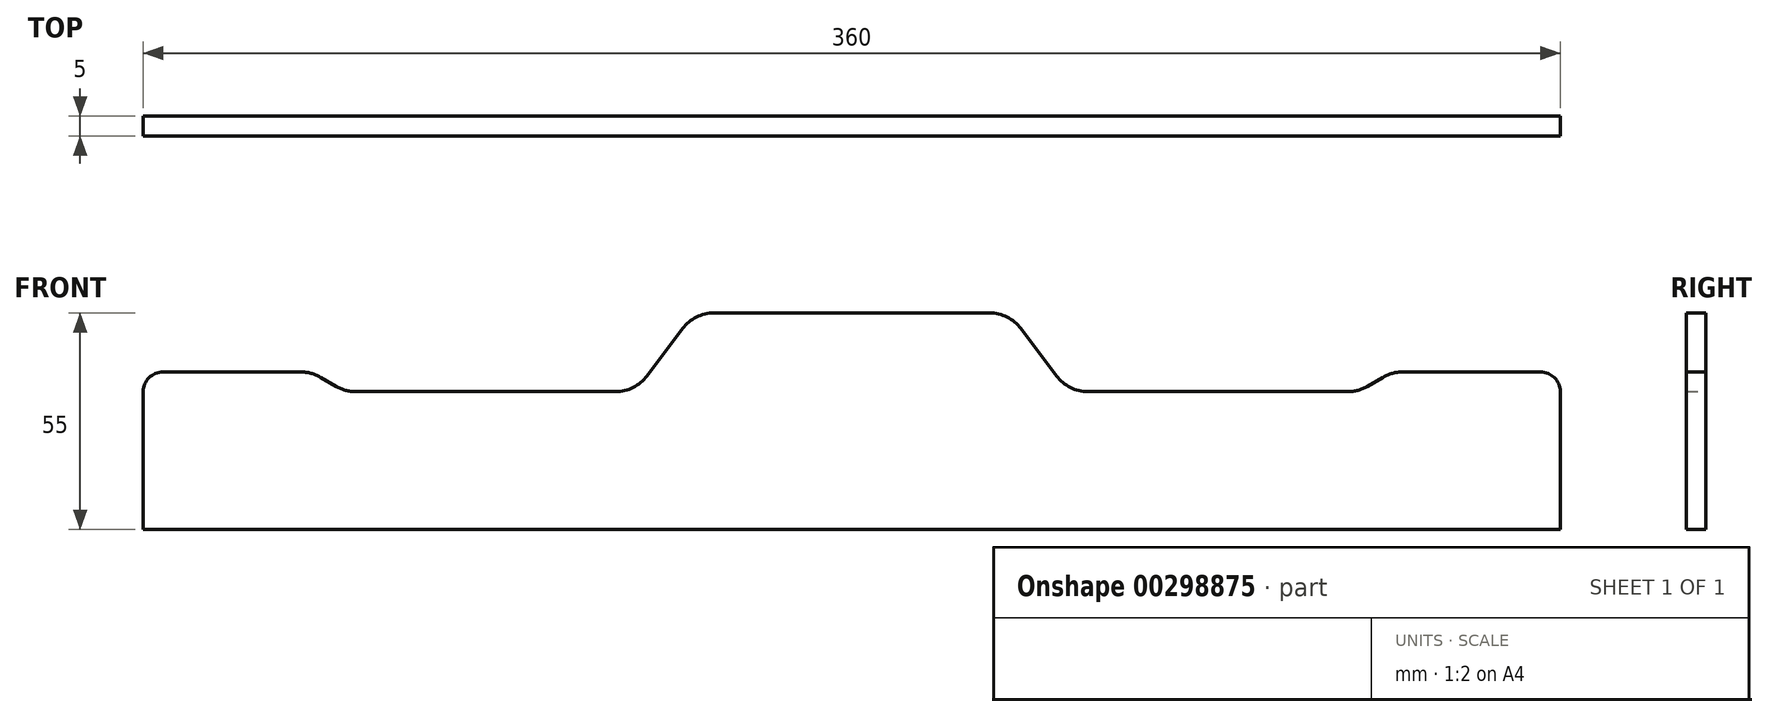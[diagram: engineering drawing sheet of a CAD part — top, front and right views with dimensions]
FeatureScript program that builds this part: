
annotation { "Feature Type Name" : "Feature", "Feature Type Description" : "" }
export const myFeature = defineFeature(function(context is Context, id is Id, definition is map)
    precondition{}
    {
        {
            var Q0;
            Q0=qCreatedBy(makeId("Front.planeOp"),FACE);
            var sketch = newSketch(context, id + "F0", { "sketchPlane" : qUnion([Q0])});
            skLineSegment(sketch, "E0.bottom", {"start": v(0, 0) * mm, "end": v(180, 0) * mm});
            skLineSegment(sketch, "E0.left", {"start": v(0, 0) * mm, "end": v(0, 35) * mm});
            skLineSegment(sketch, "E0.right", {"start": v(180, 0) * mm, "end": v(180, 55) * mm, "construction": true});
            skLineSegment(sketch, "E1", {"start": v(180, 55) * mm, "end": v(145, 55) * mm});
            skLineSegment(sketch, "E2", {"start": v(120, 35) * mm, "end": v(54, 35) * mm});
            skLineSegment(sketch, "E3", {"start": v(5, 40) * mm, "end": v(40, 40) * mm});
            skLineSegment(sketch, "E4", {"start": v(51.3, 35) * mm, "end": v(51.3, 35) * mm});
            skPoint(sketch, "E5.visualSharp", {"position": v(51.3, 40) * mm});
            skPoint(sketch, "E6.visualSharp", {"position": v(0, 40) * mm});
            skArc(sketch, "E6.filletArc", {"start": v(5, 40) * mm, "mid": v(1.46, 38.54) * mm, "end": v(0, 35) * mm});
            skArc(sketch, "E7.MirrorCS", {"start": v(355, 40) * mm, "mid": v(358.54, 38.54) * mm, "end": v(360, 35) * mm});
            skPoint(sketch, "E8.MirrorP", {"position": v(360, 40) * mm});
            skLineSegment(sketch, "E9.MirrorCS", {"start": v(360, 0) * mm, "end": v(180, 0) * mm});
            skLineSegment(sketch, "E10.MirrorCS", {"start": v(360, 0) * mm, "end": v(360, 35) * mm});
            skLineSegment(sketch, "E11.MirrorCS", {"start": v(355, 40) * mm, "end": v(317.3, 40) * mm});
            skLineSegment(sketch, "E12.MirrorCS", {"start": v(180, 55) * mm, "end": v(220, 55) * mm});
            skLineSegment(sketch, "E13.MirrorCS", {"start": v(240, 35) * mm, "end": v(308.7, 35) * mm});
            skLineSegment(sketch, "E14", {"start": v(128, 39) * mm, "end": v(137, 51) * mm});
            skPoint(sketch, "E15.visualSharp", {"position": v(140, 55) * mm});
            skArc(sketch, "E15.filletArc", {"start": v(145, 55) * mm, "mid": v(140.53, 53.94) * mm, "end": v(137, 51) * mm});
            skArc(sketch, "E16.filletArc", {"start": v(120, 35) * mm, "mid": v(124.47, 36.06) * mm, "end": v(128, 39) * mm});
            skArc(sketch, "E17.MirrorCS", {"start": v(240, 35) * mm, "mid": v(235.53, 36.06) * mm, "end": v(232, 39) * mm});
            skArc(sketch, "E18.MirrorCS", {"start": v(215, 55) * mm, "mid": v(219.47, 53.94) * mm, "end": v(223, 51) * mm});
            skPoint(sketch, "E19.MirrorP", {"position": v(220, 55) * mm});
            skLineSegment(sketch, "E20.MirrorCS", {"start": v(180, 55) * mm, "end": v(215, 55) * mm});
            skLineSegment(sketch, "E21.MirrorCS", {"start": v(180, 55) * mm, "end": v(140, 55) * mm});
            skLineSegment(sketch, "E22.MirrorCS", {"start": v(232, 39) * mm, "end": v(223, 51) * mm});
            skLineSegment(sketch, "E23", {"start": v(48.98, 36.35) * mm, "end": v(45.02, 38.65) * mm});
            skPoint(sketch, "E24.visualSharp", {"position": v(42.7, 40) * mm});
            skArc(sketch, "E24.filletArc", {"start": v(45.02, 38.65) * mm, "mid": v(42.6, 39.66) * mm, "end": v(40, 40) * mm});
            skPoint(sketch, "E25.visualSharp", {"position": v(51.3, 35) * mm});
            skArc(sketch, "E25.filletArc", {"start": v(48.98, 36.35) * mm, "mid": v(51.4, 35.34) * mm, "end": v(54, 35) * mm});
            skLineSegment(sketch, "E26.MirrorCS", {"start": v(311.02, 36.35) * mm, "end": v(314.98, 38.65) * mm});
            skArc(sketch, "E27.MirrorCS", {"start": v(314.98, 38.65) * mm, "mid": v(317.4, 39.66) * mm, "end": v(320, 40) * mm});
            skArc(sketch, "E28.MirrorCS", {"start": v(311.02, 36.35) * mm, "mid": v(308.6, 35.34) * mm, "end": v(306, 35) * mm});
            skPoint(sketch, "E29.MirrorP", {"position": v(308.7, 40) * mm});
            skLineSegment(sketch, "E30.MirrorCS", {"start": v(240, 35) * mm, "end": v(306, 35) * mm});
            skPoint(sketch, "E31.MirrorP", {"position": v(308.7, 35) * mm});
            skLineSegment(sketch, "E32.MirrorCS", {"start": v(355, 40) * mm, "end": v(320, 40) * mm});
            skPoint(sketch, "E33.MirrorP", {"position": v(317.3, 40) * mm});
            skSolve(sketch);
        }
        {
            var Q0;
            Q0 = qSketchRegion(id + "F0", true);
            extrude(context, id + "F1", {"entities" : qUnion([Q0]), "depth" : 5 * mm});
        }
    });
